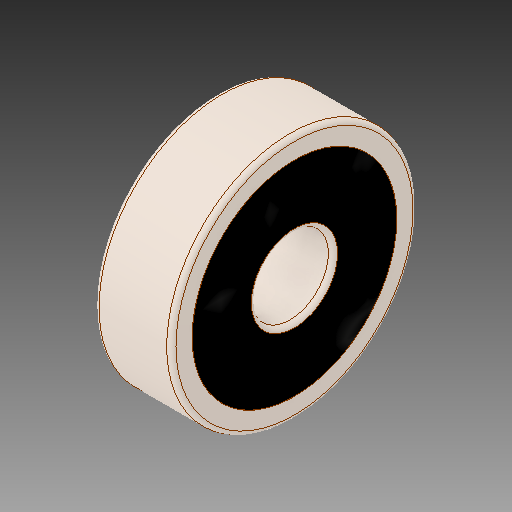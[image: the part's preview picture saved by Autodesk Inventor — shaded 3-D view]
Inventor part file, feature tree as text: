
AUTODESK INVENTOR PART (.ipt)
format: ipt  version: 2018 (Build 220112000, 112)  size: 2,075,136 bytes
history: mixed  units: mm
features: other x20, extrude x2, sketch x2, imported_body x1
ambient origin geometry x8: Origin, YZ Plane, XZ Plane, XY Plane, X Axis, Y Axis, Z Axis, Center Point
bodies: Solid1 (imported_parasolid), Solid2 (imported_parasolid), Solid3 (imported_parasolid), Solid4 (imported_parasolid), Solid5 (imported_parasolid), Solid6 (imported_parasolid), Solid7 (imported_parasolid), Solid8 (imported_parasolid), Solid9 (imported_parasolid), Solid10 (imported_parasolid), Solid11 (imported_parasolid), Solid12 (imported_parasolid), Solid13 (imported_parasolid), Solid14 (imported_parasolid), Solid15 (imported_parasolid), Solid16 (imported_parasolid), Solid17 (imported_parasolid), Solid18 (imported_parasolid), Solid19 (imported_parasolid), Solid20 (imported_parasolid)
feature tree (25):
  extrude  "Extrusion1"  Depth=0.5mm TaperAngle=0.0deg
  extrude  "Extrusion2"  [1 undecoded]
  sketch  "Sketch1"  dims[d0=0.5mm d1=0.0mm d2=0.5mm d3=0.0mm]
  sketch  "Sketch2"
  other  "SKF 625 Inner Race^SKF 625:1"
  other  "SKF 625 Outer Race^SKF 625:1"
  other  "SKF 625 Ball^SKF 625:1"
  other  "SKF 625 Ball^SKF 625:2"
  other  "SKF 625 Ball^SKF 625:3"
  other  "SKF 625 Ball^SKF 625:4"
  other  "SKF 625 Ball^SKF 625:5"
  other  "SKF 625 Ball^SKF 625:6"
  other  "SKF 625 Ball^SKF 625:7"
  other  "SKF 625 Ball^SKF 625:8"
  other  "SKF 625 Cage^SKF 625:1"
  other  "SKF 625 Cage^SKF 625:2"
  other  "SKF 625 Cage^SKF 625:3"
  other  "SKF 625 Cage^SKF 625:4"
  other  "SKF 625 Cage^SKF 625:5"
  other  "SKF 625 Cage^SKF 625:6"
  other  "SKF 625 Cage^SKF 625:7"
  other  "SKF 625 Cage^SKF 625:8"
  other  "SKF 625 Cage^SKF 625:9"
  other  "SKF 625 Cage^SKF 625:10"
  imported_body  NMx_Import_Brep_tag  [imported B-rep: ~49 faces, bbox_mm=[0.0, 10.2, 10.2]]
note: 1 required parameter value undecoded (feature->parameter linkage not recoverable at this tier; creation-order binding heuristic only, values carry confidence <= 0.55)
